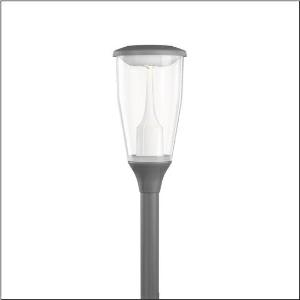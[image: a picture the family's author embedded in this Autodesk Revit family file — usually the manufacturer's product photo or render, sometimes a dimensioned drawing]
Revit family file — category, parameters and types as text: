
# Revit family: dl_11_iq___st1_2a_5xa5565mf14hp00022_149f
name_source: partatom
category: Lighting Fixtures
units: mm (PartAtom-declared; Revit-internal decimal feet)

## family parameters
Cut with Voids When Loaded = No
Host = Face
Light Source = No
Part Type = Normal
Room Calculation Point = No
Round Connector Dimension = Use Diameter
Shared = No

## types (1)
- --- (1 x LED, 4340 lm, 33.6 W, 2700K)
    Apparent Load = 34 VA
    CIE Flux Codes = 33 63 91 94 100
    Color Rendering = 70
    Color Temperature = 2700K
    Default Elevation = 1800 mm
    Description = DL 11 iQ, mast luminaire, Module 540 iQ-SR, primary light control with 3 zone facetted reflector, of plastic, silver coated, highly specular, structured, primary optical cover: cover, of PMMA, transparent, light distribution: ST1.2a, light emission: direct distribution, primary light characteristic: asymmetric, installation type: post-top, LED, High Power LED, light colour: 727, colour temperature: 2700K, control: Street-Remote, Auto-Match, Temp-Guard, Lumen-Switch, Night-Set, Smart-Wire, Light-Fading, Desk-Remote (wireless, voltage-free reading and setting of iQ features in the workshop via application-optimized NFC function/RFID function), optimised constant luminous flux control (CLO 2.0), mains connection: 220..240V, AC, 50/60Hz, connection cable pre-assembled, cable length: 5,5m, start of lifetime: 34W, end of service life: 36W, luminaire housing, upper part, of diecast aluminium, coated, Siteco® metallic grey (DB 702S), spigot size: 60mm (post-top), post-top mast mounting element, of diecast aluminium, coated, Siteco® metallic grey (DB 702S), Module 540 iQ-SR, traffic white (RAL 9016), equipment: Power, protection rating (complete): IP66, insulation class (complete): insulation class II (safety insulation), certification: CE, ENEC, ENEC+, VDE, packaging unit: 1 piece

Light Distribution: ST1.2a
    Height = 665 mm
    Lamp = 1 x LED
    Lamp Light Flux = 4340 lm
    Lamp Power = 33.6 W
    Lamp count = 1
    Length = 334 mm
    Luminous efficacy = 129 lm/W
    Manufacturer = Siteco
    ModVariant = No
    Model = 5XA5565MF14HP00022
    Number of Poles = 1
    OnlyDefault = Yes
    Power Factor = 1
    Product Name = DL 11 iQ | ST1.2a
    Product group = mast luminaire | pylon top
    ProductGroupID = 6100
    Protection Class = Protection class II
    Protection Degree = IP 66
    RLX_Detail_Level = 1
    RLX_Emergency_Light_Flux = 0 lm
    RLX_Emergency_Type = 0
    RLX_Emergency_Type_DB = No
    RlxData = <blob elided: 98161 chars, md5=0ff32498>
    Socket = socket
    Standby Power = 0 W
    System Light Flux = 4340 lm
    System Power = 34 W
    Type Comments = factory setting: luminous flux: 100 % | dim-lin: 254 | 695 mA
    Type Image = l_1258354.jpg
    URL = http://relux.com
    VarID = @adj_002613
    Voltage = 0 V
    Weight = 0.00 kg
    Width = 0 mm  [stored 0 ft]

note: [stored X ft] marks values corroborated as IEEE doubles in the binary element streams (Revit-internal decimal feet)

## geometry (parser evidence)
native form markers: Blend x4, Sweep x12
no freeform markers — native parametric forms only
